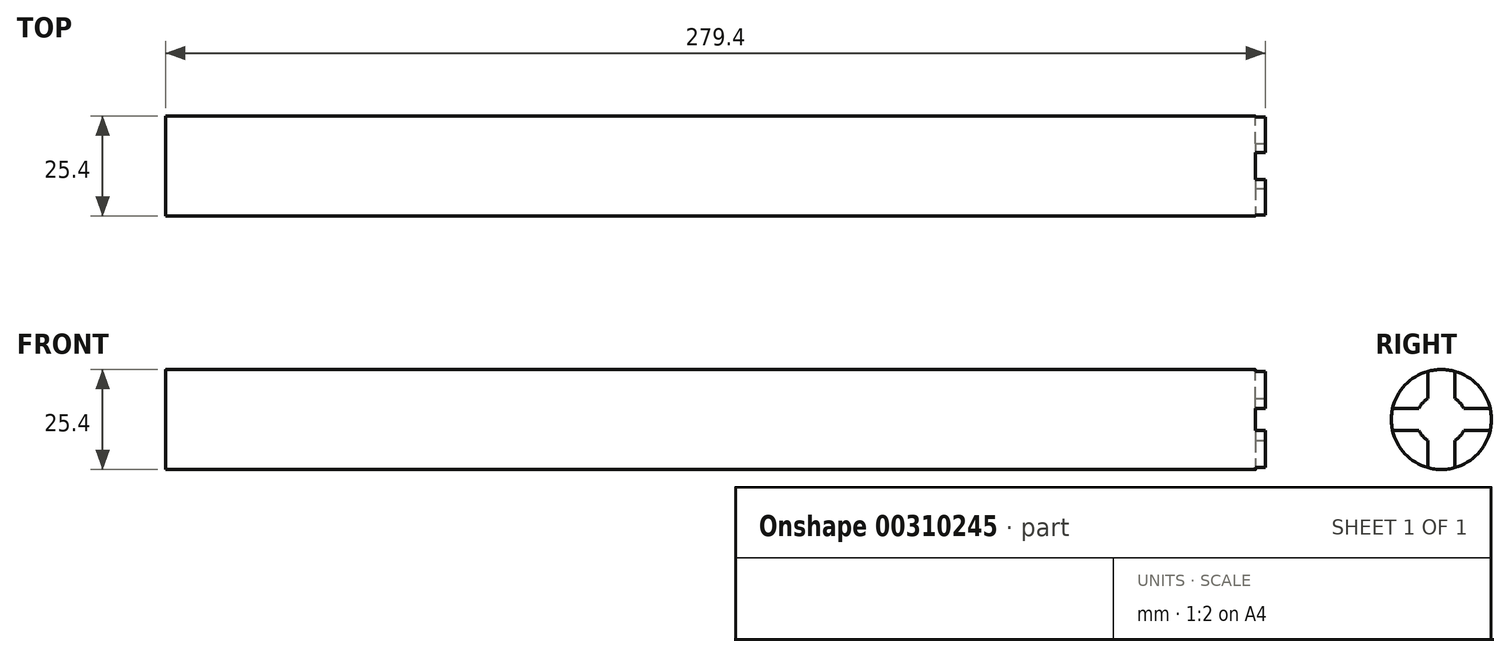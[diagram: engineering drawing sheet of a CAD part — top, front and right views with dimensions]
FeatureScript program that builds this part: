
annotation { "Feature Type Name" : "Feature", "Feature Type Description" : "" }
export const myFeature = defineFeature(function(context is Context, id is Id, definition is map)
    precondition{}
    {
        {
            var Q0;
            Q0=qCreatedBy(makeId("Right.planeOp"),FACE);
            var sketch = newSketch(context, id + "F0", { "sketchPlane" : qUnion([Q0])});
            skCircle(sketch, "E0", {"center": v(0, 0) * mm, "radius": 12.7 * mm});
            skSolve(sketch);
        }
        {
            var Q0;
            Q0 = qSketchRegion(id + "F0", true);
            extrude(context, id + "F1", {"entities" : qUnion([Q0]), "depth" : 279.4 * mm});
        }
        {
            var Q0;
            Q0=makeQuery(id+"F1.opExtrude","CAP_FACE",FACE,{"disambiguationData":[OSD([sQuery(id+"F0.wireOp",EDGE,"E0")])],"isStart":false});
            var sketch = newSketch(context, id + "F2", { "sketchPlane" : qUnion([Q0])});
            skCircle(sketch, "E1", {"center": v(0, 0) * mm, "radius": 6.35 * mm});
            skLineSegment(sketch, "E2", {"start": v(0, 37.3) * mm, "end": v(0, -49.4) * mm, "construction": true});
            skLineSegment(sketch, "E3", {"start": v(3.48, 5.31) * mm, "end": v(3.48, 26.46) * mm});
            skLineSegment(sketch, "E4", {"start": v(3.48, 26.46) * mm, "end": v(0, 26.46) * mm});
            skLineSegment(sketch, "E5", {"start": v(3.48, -5.31) * mm, "end": v(3.48, -31.88) * mm});
            skLineSegment(sketch, "E6", {"start": v(3.48, -31.88) * mm, "end": v(0, -31.88) * mm});
            skLineSegment(sketch, "E7.MirrorCS", {"start": v(-3.48, 26.46) * mm, "end": v(0, 26.46) * mm});
            skLineSegment(sketch, "E8.MirrorCS", {"start": v(-3.48, 5.31) * mm, "end": v(-3.48, 26.46) * mm});
            skLineSegment(sketch, "E9.MirrorCS", {"start": v(-3.48, -5.31) * mm, "end": v(-3.48, -31.88) * mm});
            skLineSegment(sketch, "E10.MirrorCS", {"start": v(-3.48, -31.88) * mm, "end": v(0, -31.88) * mm});
            skLineSegment(sketch, "E11", {"start": v(-24.2, 0) * mm, "end": v(41.47, 0) * mm, "construction": true});
            skLineSegment(sketch, "E12", {"start": v(-5.7, 2.8) * mm, "end": v(-29.62, 2.8) * mm});
            skLineSegment(sketch, "E13", {"start": v(-29.62, 2.8) * mm, "end": v(-29.62, 0) * mm});
            skLineSegment(sketch, "E14", {"start": v(5.7, 2.8) * mm, "end": v(28.01, 2.8) * mm});
            skLineSegment(sketch, "E15", {"start": v(28.01, 2.8) * mm, "end": v(28.01, 0) * mm});
            skLineSegment(sketch, "E16.MirrorCS", {"start": v(5.7, -2.8) * mm, "end": v(28.01, -2.8) * mm});
            skLineSegment(sketch, "E17.MirrorCS", {"start": v(28.01, -2.8) * mm, "end": v(28.01, 0) * mm});
            skLineSegment(sketch, "E18.MirrorCS", {"start": v(-5.7, -2.8) * mm, "end": v(-29.62, -2.8) * mm});
            skLineSegment(sketch, "E19.MirrorCS", {"start": v(-29.62, -2.8) * mm, "end": v(-29.62, 0) * mm});
            skSolve(sketch);
        }
        {
            var Q0;
            Q0 = qSketchRegion(id + "F2", true);
            extrude(context, id + "F3", {"entities" : qUnion([Q0]), "operationType" : NewBodyOperationType.REMOVE, "oppositeDirection" : true, "depth" : 2.54 * mm});
        }
    });
